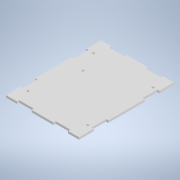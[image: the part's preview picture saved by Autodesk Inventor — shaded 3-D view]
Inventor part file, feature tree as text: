
AUTODESK INVENTOR PART (.ipt)
format: ipt  version: 2020.3 (Build 243373000, 373)  size: 175,616 bytes
history: native  units: mm
features: extrude x3, sketch x2, other x1
ambient origin geometry x8: Origin, YZ Plane, XZ Plane, XY Plane, X Axis, Y Axis, Z Axis, Center Point
bodies: Solid1 (feature_tree)
feature tree (6):
  extrude  "Baseplate"  Depth=3.0mm
  extrude  "Extrusion2"  Depth=20.0mm
  extrude  "PCB Mounting"  Depth=50.0mm
  sketch  "Sketch1"  dims[d3=0.0mm d4=3.0mm]
  other  "TabsSketch"
  sketch  "Sketch3"  dims[d7=20.0mm d8=20.0mm d10=50.0mm d11=3.0mm d12=3.0mm d13=20.0mm d14=20.0mm d16=30.0mm d17=0.0mm d18=0.0mm d20=3.2mm d21=3.2mm d22=3.2mm d23=89.5mm d24=81.5mm d25=89.5mm d26=81.5mm d27=10.0mm d28=10.0mm d29=20.0mm d30=20.0mm d31=61.5mm d32=68.0mm d33=3.2mm d34=0.0mm d35=0.0mm]
